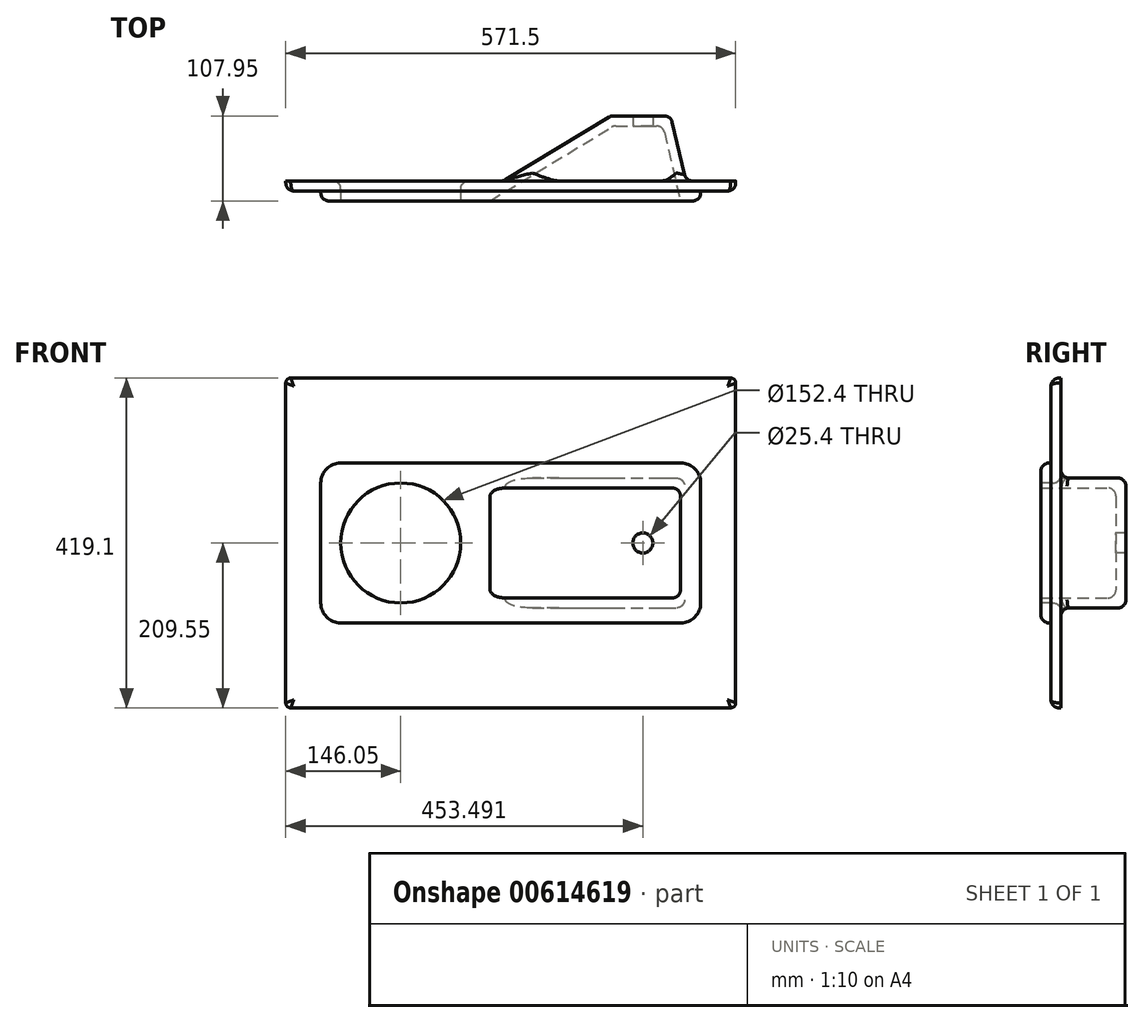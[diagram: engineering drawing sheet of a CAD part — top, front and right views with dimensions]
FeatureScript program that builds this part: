
annotation { "Feature Type Name" : "Feature", "Feature Type Description" : "" }
export const myFeature = defineFeature(function(context is Context, id is Id, definition is map)
    precondition{}
    {
        {
            var Q0;
            Q0=qCreatedBy(makeId("Front.planeOp"),FACE);
            var sketch = newSketch(context, id + "F0", { "sketchPlane" : qUnion([Q0])});
            skLineSegment(sketch, "E0.bottom", {"start": v(6.35, 0) * mm, "end": v(565.15, 0) * mm});
            skLineSegment(sketch, "E0.top", {"start": v(6.35, 419.1) * mm, "end": v(565.15, 419.1) * mm});
            skLineSegment(sketch, "E0.left", {"start": v(0, 6.35) * mm, "end": v(0, 412.75) * mm});
            skLineSegment(sketch, "E0.right", {"start": v(571.5, 6.35) * mm, "end": v(571.5, 412.75) * mm});
            skPoint(sketch, "E1.visualSharp", {"position": v(0, 419.1) * mm});
            skArc(sketch, "E1.filletArc", {"start": v(6.35, 419.1) * mm, "mid": v(1.86, 417.24) * mm, "end": v(0, 412.75) * mm});
            skPoint(sketch, "E2.visualSharp", {"position": v(571.5, 419.1) * mm});
            skArc(sketch, "E2.filletArc", {"start": v(571.5, 412.75) * mm, "mid": v(569.64, 417.24) * mm, "end": v(565.15, 419.1) * mm});
            skPoint(sketch, "E3.visualSharp", {"position": v(0, 0) * mm});
            skArc(sketch, "E3.filletArc", {"start": v(0, 6.35) * mm, "mid": v(1.86, 1.86) * mm, "end": v(6.35, 0) * mm});
            skPoint(sketch, "E4.visualSharp", {"position": v(571.5, 0) * mm});
            skArc(sketch, "E4.filletArc", {"start": v(565.15, 0) * mm, "mid": v(569.64, 1.86) * mm, "end": v(571.5, 6.35) * mm});
            skSolve(sketch);
        }
        {
            var Q0;
            Q0 = qSketchRegion(id + "F0", true);
            extrude(context, id + "F1", {"entities" : qUnion([Q0]), "depth" : 12.7 * mm, "offsetDistance" : 25.4 * mm});
        }
        {
            var Q0;
            Q0=makeQuery(id+"F1.opExtrude","CAP_FACE",FACE,{"disambiguationData":[OSD([sQuery(id+"F0.wireOp",EDGE,"E0.bottom"),sQuery(id+"F0.wireOp",EDGE,"E0.top"),sQuery(id+"F0.wireOp",EDGE,"E0.left"),sQuery(id+"F0.wireOp",EDGE,"E0.right"),sQuery(id+"F0.wireOp",EDGE,"E1.filletArc"),sQuery(id+"F0.wireOp",EDGE,"E2.filletArc"),sQuery(id+"F0.wireOp",EDGE,"E3.filletArc"),sQuery(id+"F0.wireOp",EDGE,"E4.filletArc")])],"isStart":false});
            var sketch = newSketch(context, id + "F2", { "sketchPlane" : qUnion([Q0])});
            skLineSegment(sketch, "E5.bottom", {"start": v(69.85, 311.15) * mm, "end": v(501.65, 311.15) * mm});
            skLineSegment(sketch, "E5.top", {"start": v(69.85, 107.95) * mm, "end": v(501.65, 107.95) * mm});
            skLineSegment(sketch, "E5.left", {"start": v(44.45, 285.75) * mm, "end": v(44.45, 133.35) * mm});
            skLineSegment(sketch, "E5.right", {"start": v(527.05, 285.75) * mm, "end": v(527.05, 133.35) * mm});
            skPoint(sketch, "E6.visualSharp", {"position": v(44.45, 311.15) * mm});
            skArc(sketch, "E6.filletArc", {"start": v(69.85, 311.15) * mm, "mid": v(51.89, 303.71) * mm, "end": v(44.45, 285.75) * mm});
            skPoint(sketch, "E7.visualSharp", {"position": v(44.45, 107.95) * mm});
            skArc(sketch, "E7.filletArc", {"start": v(44.45, 133.35) * mm, "mid": v(51.89, 115.39) * mm, "end": v(69.85, 107.95) * mm});
            skPoint(sketch, "E8.visualSharp", {"position": v(527.05, 107.95) * mm});
            skArc(sketch, "E8.filletArc", {"start": v(501.65, 107.95) * mm, "mid": v(519.61, 115.39) * mm, "end": v(527.05, 133.35) * mm});
            skPoint(sketch, "E9.visualSharp", {"position": v(527.05, 311.15) * mm});
            skArc(sketch, "E9.filletArc", {"start": v(527.05, 285.75) * mm, "mid": v(519.61, 303.71) * mm, "end": v(501.65, 311.15) * mm});
            skSolve(sketch);
        }
        {
            var Q0;
            Q0=makeQuery(id+"F2.imprint","IMPRINT",FACE,{"disambiguationData":[TD([[makeQuery(id+"F2.imprint","IMPRINT",EDGE,{"derivedFrom":sQuery(id+"F2.wireOp",EDGE,"E5.bottom")}),-1.0]])]});
            extrude(context, id + "F3", {"entities" : qUnion([Q0]), "operationType" : NewBodyOperationType.ADD, "depth" : 12.7 * mm, "offsetDistance" : 25.4 * mm});
        }
        {
            var Q0;
            Q0=makeQuery(id+"F3.opExtrude","CAP_FACE",FACE,{"disambiguationData":[OSD([sQuery(id+"F2.wireOp",EDGE,"E5.bottom"),sQuery(id+"F2.wireOp",EDGE,"E5.top"),sQuery(id+"F2.wireOp",EDGE,"E5.left"),sQuery(id+"F2.wireOp",EDGE,"E5.right"),sQuery(id+"F2.wireOp",EDGE,"E6.filletArc"),sQuery(id+"F2.wireOp",EDGE,"E7.filletArc"),sQuery(id+"F2.wireOp",EDGE,"E8.filletArc"),sQuery(id+"F2.wireOp",EDGE,"E9.filletArc")])],"isStart":false});
            var sketch = newSketch(context, id + "F4", { "sketchPlane" : qUnion([Q0])});
            skCircle(sketch, "E10", {"center": v(146.05, 209.55) * mm, "radius": 76.2 * mm});
            skSolve(sketch);
        }
        {
            var Q0;
            Q0=makeQuery(id+"F4.imprint","IMPRINT",FACE,{"disambiguationData":[TD([[makeQuery(id+"F4.imprint","IMPRINT",EDGE,{"derivedFrom":sQuery(id+"F4.wireOp",EDGE,"E10")}),1.0]])]});
            extrude(context, id + "F5", {"entities" : qUnion([Q0]), "operationType" : NewBodyOperationType.REMOVE, "endBound" : BoundingType.THROUGH_ALL, "oppositeDirection" : true, "depth" : 25.4 * mm, "offsetDistance" : 25.4 * mm});
        }
        {
            var Q0;
            Q0=makeQuery(id+"F3.opExtrude","SWEPT_FACE",FACE,{"disambiguationData":[OSD([sQuery(id+"F2.wireOp",EDGE,"E5.top")])]});
            var Q1;
            Q1=makeQuery(id+"F3.opExtrude","SWEPT_FACE",FACE,{"disambiguationData":[OSD([sQuery(id+"F2.wireOp",EDGE,"E5.bottom")])]});
            cPlane(context, id + "F6", {"entities" : qUnion([Q0, Q1]), "cplaneType" : CPlaneType.MID_PLANE, "offset" : 25.4 * mm, "width" : 152.4 * mm, "height" : 152.4 * mm});
        }
        {
            var Q0;
            Q0=qCreatedBy(id+"F6.planeOp",FACE);
            var sketch = newSketch(context, id + "F7", { "sketchPlane" : qUnion([Q0])});
            skLineSegment(sketch, "E11", {"start": v(488.95, -82.55) * mm, "end": v(514.35, 25.4) * mm});
            skLineSegment(sketch, "E12", {"start": v(514.35, 25.4) * mm, "end": v(234.95, 25.4) * mm});
            skLineSegment(sketch, "E13", {"start": v(234.95, 25.4) * mm, "end": v(412.75, -82.55) * mm});
            skLineSegment(sketch, "E14", {"start": v(412.75, -82.55) * mm, "end": v(488.95, -82.55) * mm});
            skSolve(sketch);
        }
        {
            var Q0;
            Q0 = qSketchRegion(id + "F7", true);
            extrude(context, id + "F8", {"entities" : qUnion([Q0]), "operationType" : NewBodyOperationType.ADD, "endBound" : BoundingType.SYMMETRIC, "depth" : 165.1 * mm, "offsetDistance" : 25.4 * mm});
        }
        {
            var Q0;
            Q0=qCreatedBy(id+"F6.planeOp",FACE);
            var sketch = newSketch(context, id + "F9", { "sketchPlane" : qUnion([Q0])});
            skLineSegment(sketch, "E15", {"start": v(259.42, 25.4) * mm, "end": v(416.3, -69.85) * mm});
            skLineSegment(sketch, "E16", {"start": v(416.3, -69.85) * mm, "end": v(478.9, -69.85) * mm});
            skLineSegment(sketch, "E17", {"start": v(478.9, -69.85) * mm, "end": v(501.3, 25.4) * mm});
            skLineSegment(sketch, "E18", {"start": v(501.3, 25.4) * mm, "end": v(259.42, 25.4) * mm});
            skSolve(sketch);
        }
        {
            var Q0;
            Q0 = qSketchRegion(id + "F9", true);
            extrude(context, id + "F10", {"entities" : qUnion([Q0]), "operationType" : NewBodyOperationType.REMOVE, "endBound" : BoundingType.SYMMETRIC, "oppositeDirection" : true, "depth" : 139.7 * mm, "offsetDistance" : 25.4 * mm});
        }
        {
            var Q0;
            Q0=makeQuery(id+"F10.boolean.opBoolean","COPY",FACE,{"derivedFrom":makeQuery(id+"F10.opExtrude","SWEPT_FACE",FACE,{"disambiguationData":[OSD([sQuery(id+"F9.wireOp",EDGE,"E16")])]})});
            var sketch = newSketch(context, id + "F11", { "sketchPlane" : qUnion([Q0])});
            skCircle(sketch, "E19", {"center": v(453.5, 209.55) * mm, "radius": 12.7 * mm});
            skSolve(sketch);
        }
        {
            var Q0;
            Q0=makeQuery(id+"F11.imprint","IMPRINT",FACE,{"disambiguationData":[TD([[makeQuery(id+"F11.imprint","IMPRINT",EDGE,{"derivedFrom":sQuery(id+"F11.wireOp",EDGE,"E19")}),1.0]])]});
            extrude(context, id + "F12", {"entities" : qUnion([Q0]), "operationType" : NewBodyOperationType.REMOVE, "endBound" : BoundingType.THROUGH_ALL, "oppositeDirection" : true, "depth" : 25.4 * mm, "offsetDistance" : 25.4 * mm});
        }
        {
            var Q0;
            Q0=makeQuery(id+"F1.opExtrude","CAP_EDGE",EDGE,{"disambiguationData":[OSD([sQuery(id+"F0.wireOp",EDGE,"E0.top")])],"isStart":false});
            var Q1;
            Q1=makeQuery(id+"F1.opExtrude","CAP_EDGE",EDGE,{"disambiguationData":[OSD([sQuery(id+"F0.wireOp",EDGE,"E0.left")])],"isStart":false});
            var Q2;
            Q2=makeQuery(id+"F1.opExtrude","CAP_EDGE",EDGE,{"disambiguationData":[OSD([sQuery(id+"F0.wireOp",EDGE,"E0.right")])],"isStart":false});
            var Q3;
            Q3=makeQuery(id+"F1.opExtrude","CAP_EDGE",EDGE,{"disambiguationData":[OSD([sQuery(id+"F0.wireOp",EDGE,"E0.bottom")])],"isStart":false});
            var Q4;
            Q4=makeQuery(id+"F3.opExtrude","CAP_EDGE",EDGE,{"disambiguationData":[OSD([sQuery(id+"F2.wireOp",EDGE,"E6.filletArc")])],"isStart":false});
            var Q5;
            Q5=makeQuery(id+"F5.boolean.opBoolean","COPY",EDGE,{"derivedFrom":makeQuery(id+"F5.opExtrude","CAP_EDGE",EDGE,{"disambiguationData":[OSD([sQuery(id+"F4.wireOp",EDGE,"E10")])],"isStart":true})});
            var Q6;
            Q6=makeQuery(id+"F5.boolean.opBoolean","INTERSECT",EDGE,{"derivedFrom":[makeQuery(id+"F1.opExtrude","CAP_FACE",FACE,{"disambiguationData":[OSD([sQuery(id+"F0.wireOp",EDGE,"E0.bottom"),sQuery(id+"F0.wireOp",EDGE,"E0.top"),sQuery(id+"F0.wireOp",EDGE,"E0.left"),sQuery(id+"F0.wireOp",EDGE,"E0.right"),sQuery(id+"F0.wireOp",EDGE,"E1.filletArc"),sQuery(id+"F0.wireOp",EDGE,"E2.filletArc"),sQuery(id+"F0.wireOp",EDGE,"E3.filletArc"),sQuery(id+"F0.wireOp",EDGE,"E4.filletArc")])],"isStart":true}),makeQuery(id+"F5.opExtrude","SWEPT_FACE",FACE,{"disambiguationData":[OSD([sQuery(id+"F4.wireOp",EDGE,"E10")])]})]});
            var Q7;
            Q7=makeQuery(id+"F10.boolean.opBoolean","COPY",EDGE,{"derivedFrom":makeQuery(id+"F10.opExtrude","SWEPT_EDGE",EDGE,{"disambiguationData":[OSD([sQuery(id+"F9.wireOp",EDGE,"E15"),sQuery(id+"F9.wireOp",EDGE,"E18")])]})});
            var Q8;
            Q8=makeQuery(id+"F10.boolean.opBoolean","COPY",EDGE,{"derivedFrom":makeQuery(id+"F10.opExtrude","CAP_EDGE",EDGE,{"disambiguationData":[OSD([sQuery(id+"F9.wireOp",EDGE,"E18")])],"isStart":false})});
            var Q9;
            Q9=makeQuery(id+"F10.boolean.opBoolean","COPY",EDGE,{"derivedFrom":makeQuery(id+"F10.opExtrude","CAP_EDGE",EDGE,{"disambiguationData":[OSD([sQuery(id+"F9.wireOp",EDGE,"E16")])],"isStart":false})});
            var Q10;
            Q10=makeQuery(id+"F10.boolean.opBoolean","COPY",EDGE,{"derivedFrom":makeQuery(id+"F10.opExtrude","CAP_EDGE",EDGE,{"disambiguationData":[OSD([sQuery(id+"F9.wireOp",EDGE,"E17")])],"isStart":false})});
            var Q11;
            Q11=makeQuery(id+"F10.boolean.opBoolean","COPY",EDGE,{"derivedFrom":makeQuery(id+"F10.opExtrude","SWEPT_EDGE",EDGE,{"disambiguationData":[OSD([sQuery(id+"F9.wireOp",EDGE,"E17"),sQuery(id+"F9.wireOp",EDGE,"E18")])]})});
            var Q12;
            Q12=makeQuery(id+"F10.boolean.opBoolean","COPY",EDGE,{"derivedFrom":makeQuery(id+"F10.opExtrude","CAP_EDGE",EDGE,{"disambiguationData":[OSD([sQuery(id+"F9.wireOp",EDGE,"E18")])],"isStart":true})});
            var Q13;
            Q13=makeQuery(id+"F10.boolean.opBoolean","COPY",EDGE,{"derivedFrom":makeQuery(id+"F10.opExtrude","SWEPT_EDGE",EDGE,{"disambiguationData":[OSD([sQuery(id+"F9.wireOp",EDGE,"E15"),sQuery(id+"F9.wireOp",EDGE,"E16")])]})});
            var Q14;
            Q14=makeQuery(id+"F10.boolean.opBoolean","COPY",EDGE,{"derivedFrom":makeQuery(id+"F10.opExtrude","CAP_EDGE",EDGE,{"disambiguationData":[OSD([sQuery(id+"F9.wireOp",EDGE,"E15")])],"isStart":false})});
            var Q15;
            Q15=makeQuery(id+"F10.boolean.opBoolean","COPY",EDGE,{"derivedFrom":makeQuery(id+"F10.opExtrude","SWEPT_EDGE",EDGE,{"disambiguationData":[OSD([sQuery(id+"F9.wireOp",EDGE,"E16"),sQuery(id+"F9.wireOp",EDGE,"E17")])]})});
            var Q16;
            Q16=makeQuery(id+"F10.boolean.opBoolean","COPY",EDGE,{"derivedFrom":makeQuery(id+"F10.opExtrude","CAP_EDGE",EDGE,{"disambiguationData":[OSD([sQuery(id+"F9.wireOp",EDGE,"E16")])],"isStart":true})});
            var Q17;
            Q17=makeQuery(id+"F10.boolean.opBoolean","COPY",EDGE,{"derivedFrom":makeQuery(id+"F10.opExtrude","CAP_EDGE",EDGE,{"disambiguationData":[OSD([sQuery(id+"F9.wireOp",EDGE,"E17")])],"isStart":true})});
            var Q18;
            Q18=makeQuery(id+"F10.boolean.opBoolean","COPY",EDGE,{"derivedFrom":makeQuery(id+"F10.opExtrude","CAP_EDGE",EDGE,{"disambiguationData":[OSD([sQuery(id+"F9.wireOp",EDGE,"E15")])],"isStart":true})});
            fillet(context, id + "F13", {"entities" : qUnion([Q0, Q1, Q2, Q3, Q4, Q5, Q6, Q7, Q8, Q9, Q10, Q11, Q12, Q13, Q14, Q15, Q16, Q17, Q18]), "radius" : 10.16 * mm, "tangentPropagation" : true, "allowEdgeOverflow" : false});
        }
        {
            var Q0;
            Q0=makeQuery(id+"F8.opExtrude","CAP_EDGE",EDGE,{"disambiguationData":[OSD([sQuery(id+"F7.wireOp",EDGE,"E13")])],"isStart":false});
            var Q1;
            Q1=makeQuery(id+"F8.opExtrude","CAP_EDGE",EDGE,{"disambiguationData":[OSD([sQuery(id+"F7.wireOp",EDGE,"E14")])],"isStart":false});
            var Q2;
            Q2=makeQuery(id+"F8.opExtrude","CAP_EDGE",EDGE,{"disambiguationData":[OSD([sQuery(id+"F7.wireOp",EDGE,"E11")])],"isStart":false});
            var Q3;
            Q3=makeQuery(id+"F8.boolean.opBoolean","INTERSECT",EDGE,{"derivedFrom":[makeQuery(id+"F1.opExtrude","CAP_FACE",FACE,{"disambiguationData":[OSD([sQuery(id+"F0.wireOp",EDGE,"E0.bottom"),sQuery(id+"F0.wireOp",EDGE,"E0.top"),sQuery(id+"F0.wireOp",EDGE,"E0.left"),sQuery(id+"F0.wireOp",EDGE,"E0.right"),sQuery(id+"F0.wireOp",EDGE,"E1.filletArc"),sQuery(id+"F0.wireOp",EDGE,"E2.filletArc"),sQuery(id+"F0.wireOp",EDGE,"E3.filletArc"),sQuery(id+"F0.wireOp",EDGE,"E4.filletArc")])],"isStart":true}),makeQuery(id+"F8.opExtrude","SWEPT_FACE",FACE,{"disambiguationData":[OSD([sQuery(id+"F7.wireOp",EDGE,"E11")])]})]});
            var Q4;
            Q4=makeQuery(id+"F8.opExtrude","SWEPT_EDGE",EDGE,{"disambiguationData":[OSD([sQuery(id+"F7.wireOp",EDGE,"E11"),sQuery(id+"F7.wireOp",EDGE,"E14")])]});
            var Q5;
            Q5=makeQuery(id+"F8.opExtrude","SWEPT_EDGE",EDGE,{"disambiguationData":[OSD([sQuery(id+"F7.wireOp",EDGE,"E13"),sQuery(id+"F7.wireOp",EDGE,"E14")])]});
            var Q6;
            Q6=makeQuery(id+"F8.boolean.opBoolean","INTERSECT",EDGE,{"derivedFrom":[makeQuery(id+"F1.opExtrude","CAP_FACE",FACE,{"disambiguationData":[OSD([sQuery(id+"F0.wireOp",EDGE,"E0.bottom"),sQuery(id+"F0.wireOp",EDGE,"E0.top"),sQuery(id+"F0.wireOp",EDGE,"E0.left"),sQuery(id+"F0.wireOp",EDGE,"E0.right"),sQuery(id+"F0.wireOp",EDGE,"E1.filletArc"),sQuery(id+"F0.wireOp",EDGE,"E2.filletArc"),sQuery(id+"F0.wireOp",EDGE,"E3.filletArc"),sQuery(id+"F0.wireOp",EDGE,"E4.filletArc")])],"isStart":true}),makeQuery(id+"F8.opExtrude","SWEPT_FACE",FACE,{"disambiguationData":[OSD([sQuery(id+"F7.wireOp",EDGE,"E13")])]})]});
            var Q7;
            Q7=makeQuery(id+"F8.opExtrude","CAP_EDGE",EDGE,{"disambiguationData":[OSD([sQuery(id+"F7.wireOp",EDGE,"E13")])],"isStart":true});
            var Q8;
            Q8=makeQuery(id+"F8.opExtrude","CAP_EDGE",EDGE,{"disambiguationData":[OSD([sQuery(id+"F7.wireOp",EDGE,"E14")])],"isStart":true});
            var Q9;
            Q9=makeQuery(id+"F8.opExtrude","CAP_EDGE",EDGE,{"disambiguationData":[OSD([sQuery(id+"F7.wireOp",EDGE,"E11")])],"isStart":true});
            fillet(context, id + "F14", {"entities" : qUnion([Q0, Q1, Q2, Q3, Q4, Q5, Q6, Q7, Q8, Q9]), "radius" : 10.16 * mm, "tangentPropagation" : true, "allowEdgeOverflow" : false});
        }
    });
